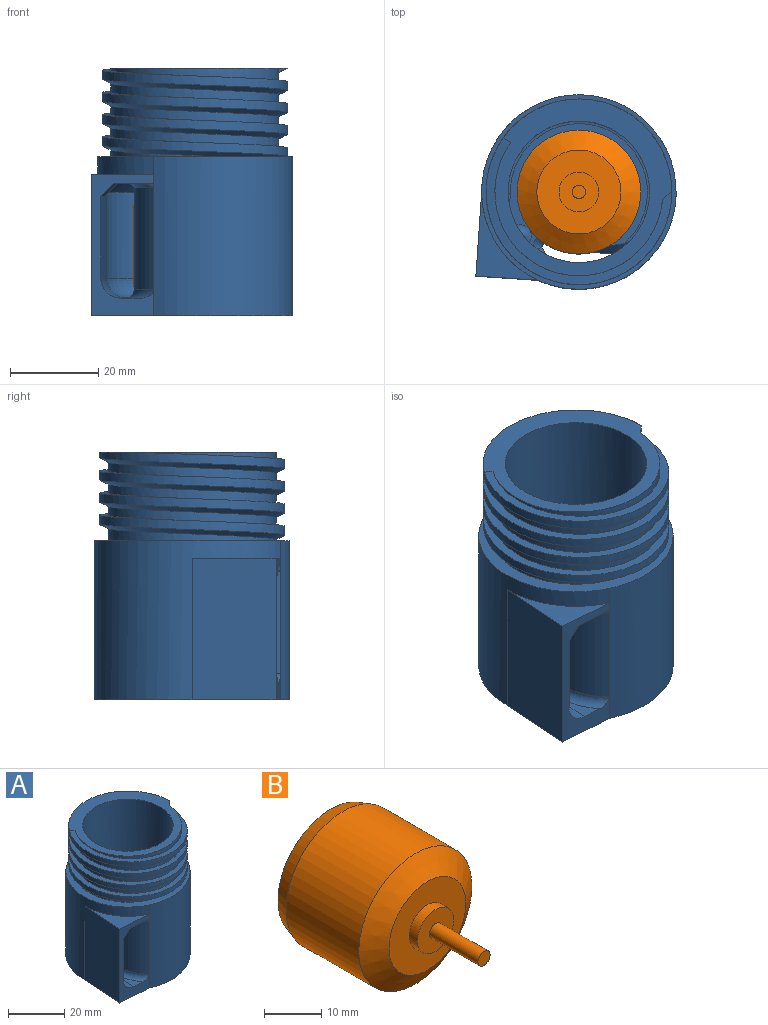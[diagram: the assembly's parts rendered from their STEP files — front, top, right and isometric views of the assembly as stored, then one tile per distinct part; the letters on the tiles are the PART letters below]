
ASSEMBLY  parts=2 mates=1
PART A: 61 faces, bbox 45.4x48.6x56.4 mm
  f0: cylinder r=22mm len=2.45mm, axis (0,0,-1), area 1.4mm2, adj f3,f28,f59
  f1: cylinder r=22mm len=44mm, axis (0,0,-1), area 4176.6mm2, adj f8,f12,f14,f19,f20,f28,f47
  f2: plane 8.06x4.55mm, normal (0.71,-0.05,-0.71), area 44.5mm2, adj f9,f21,f50,f58
  f3: cone r=18mm half-angle=45deg, axis (0,0,1), area 14.6mm2, adj f0,f4,f27,f59
  f4: cone r=3.5mm half-angle=45deg, axis (0,0,1), area 5.8mm2, adj f3,f9,f30,f49,f57,f58,f59
  f5: plane 0.1x0.05mm, normal (0,-1,0), area 0mm2, adj f52,f53,f54
  f6: bspline ~48.5x42mm, area 903.6mm2, adj f7,f51,f52,f55
  f7: cylinder r=21mm len=42mm, axis (0,0,-1), area 1025.8mm2, adj f6,f8,f52,f53,f55
  f8: plane 44x44mm, normal (0,0,1), area 357.7mm2, adj f1,f7,f12,f28,f51,f53,f55
  f9: plane 7.94x1.97mm, normal (0,0,-1), area 5.8mm2, adj f2,f4,f49,f58
  f10: plane 0.48x0.36mm, normal (0,0,1), area 0mm2, adj f26,f30,f49
  f11: plane 0.02x0mm, normal (0,0,1), area 0mm2, adj f12,f20,f28
  f12: plane 32x0mm, normal (-1,0,0), area 0mm2, adj f1,f8,f11,f28
  f13: plane 35.26x32.31mm, normal (0,0,1), area 647.2mm2, adj f15,f16,f17,f18,f20,f29,f35,f36
  f14: plane 45.3x44mm, normal (0,0,-1), area 1423.8mm2, adj f1,f15,f16,f17,f18,f19,f20,f22
  f15: cylinder r=2.12mm len=4.25mm, axis (0,0,1), area 53.4mm2, adj f13,f14
  f16: cylinder r=2.12mm len=4.25mm, axis (0,0,1), area 53.4mm2, adj f13,f14
  f17: cylinder r=2.12mm len=4.25mm, axis (0,0,1), area 53.4mm2, adj f13,f14
  f18: cylinder r=2.12mm len=4.25mm, axis (0,0,1), area 53.4mm2, adj f13,f14
  f19: plane 32x19mm, normal (-1,0.07,0), area 609.3mm2, adj f1,f14,f20,f47
  f20: plane 32x14.03mm, normal (-0.07,-1,0), area 146.6mm2, adj f1,f11,f13,f14,f19,f21,f28,f36
  f21: plane 19.5x19mm, normal (1,-0.07,0), area 360mm2, adj f2,f20,f22,f36,f58,f60
  f22: cylinder r=20mm len=40mm, axis (0,0,-1), area 1992.3mm2, adj f14,f21,f29,f33,f34,f35,f44,f50
  f23: cylinder r=15mm len=11.2mm, axis (0,0,1), area 24.3mm2, adj f14,f31,f34,f38,f39
  f24: cylinder r=14mm len=11.1mm, axis (0,0,1), area 23.7mm2, adj f14,f31,f32,f41
  f25: cylinder r=15mm len=8.24mm, axis (0,0,1), area 23.4mm2, adj f14,f32,f33,f43
  f26: plane 26.84x0.4mm, normal (0.82,0.57,0), area 11.6mm2, adj f10,f29,f30,f46
  f27: cylinder r=15mm len=23mm, axis (0,0,-1), area 259.8mm2, adj f3,f28,f30,f45
  f28: plane 32x0.02mm, normal (-0.01,-1,0), area 0.1mm2, adj f0,f1,f8,f11,f12,f20,f27,f45
  f29: cylinder r=15mm len=29.95mm, axis (0,0,-1), area 443.9mm2, adj f13,f22,f26,f43,f44,f46,f50
  f30: cylinder r=0.5mm len=26mm, axis (0,0,-1), area 30.1mm2, adj f4,f10,f26,f27,f46,f49
  f31: cylinder r=0.5mm len=2.04mm, axis (0,0,-1), area 0.5mm2, adj f14,f23,f24,f40
  f32: cylinder r=0.5mm len=2.04mm, axis (0,0,1), area 2.6mm2, adj f14,f24,f25,f42
  f33: cylinder r=0.5mm len=2.04mm, axis (0,0,-1), area 0.4mm2, adj f14,f22,f25,f44
  f34: cylinder r=0.5mm len=8.5mm, axis (0,0,1), area 6.2mm2, adj f14,f22,f23,f37
  f35: torus R=15.5mm, axis (0,0,1), area 489mm2, adj f13,f22,f36,f37,f38
  f36: cylinder r=4.5mm len=19.48mm, axis (0.07,1,0), area 135.2mm2, adj f13,f20,f21,f35
  f37: bspline ~6.22x3.3mm, area 7.5mm2, adj f34,f35,f38
  f38: bspline ~4.7x3.72mm, area 12.2mm2, adj f23,f35,f37,f39
  f39: cone r=13.04mm half-angle=45deg, axis (0,0,-1), area 18.2mm2, adj f13,f23,f38,f40
  f40: cone r=2.46mm half-angle=45deg, axis (0,0,1), area 2mm2, adj f13,f31,f39,f41
  f41: cone r=12.04mm half-angle=45deg, axis (0,0,-1), area 29.8mm2, adj f13,f24,f40,f42
  f42: cone r=2.46mm half-angle=45deg, axis (0,0,1), area 10.6mm2, adj f13,f32,f41,f43
  f43: cone r=15mm half-angle=45deg, axis (0,0,1), area 22.2mm2, adj f13,f25,f29,f42,f44
  f44: cone r=2.46mm half-angle=45deg, axis (0,0,1), area 0mm2, adj f22,f29,f33,f43
  f45: torus R=17mm, axis (0,0,1), area 34.7mm2, adj f13,f20,f27,f28,f46
  f46: torus R=2.5mm, axis (0,0,1), area 14.2mm2, adj f13,f26,f29,f30,f45
  f47: plane 19.95x14.03mm, normal (0,0,1), area 78.4mm2, adj f1,f19,f20,f56
  f48: extruded ~5.2x5.2mm, area 64.3mm2, adj f13,f14
  f49: cylinder r=16mm len=32mm, axis (0,0,-1), area 2417.7mm2, adj f4,f9,f10,f30,f50,f52
  f50: cone r=20mm half-angle=45deg, axis (0,0,-1), area 525.2mm2, adj f2,f22,f29,f49
  f51: cylinder r=19mm len=38mm, axis (0,0,-1), area 1010.4mm2, adj f6,f8,f52,f53,f54,f55
  f52: plane 40x40mm, normal (0,0,1), area 432.3mm2, adj f5,f6,f7,f49,f51,f54
  f53: bspline ~48.5x42mm, area 1098.8mm2, adj f5,f7,f8,f51,f54
  f54: plane 2.09x1.91mm, normal (0.67,-0.74,0), area 1.4mm2, adj f5,f51,f52,f53
  f55: plane 2.11x2mm, normal (0,0.71,0.71), area 5.7mm2, adj f6,f7,f8,f51
  f56: cylinder r=15mm len=2mm, axis (0,0,-1), area 0mm2, adj f20,f28,f47,f59
  f57: cylinder r=15mm len=0.05mm, axis (0,0,-1), area 0mm2, adj f4,f58,f59
  f58: plane 6.83x5mm, normal (0.07,1,0), area 7.4mm2, adj f2,f4,f9,f21,f57,f59,f60
  f59: plane 11.84x9.03mm, normal (0,0,-1), area 50mm2, adj f0,f3,f4,f20,f56,f57,f58,f60
  f60: plane 11.43x3.76mm, normal (0.71,-0.05,-0.71), area 47.7mm2, adj f20,f21,f58,f59
PART B: 17 faces, bbox 28x38x28 mm
  f0: plane 3x3mm, normal (0,-1,0), area 7.1mm2, adj f1
  f1: cylinder r=1.5mm len=12mm, axis (0,1,0), area 113.1mm2, adj f0,f2
  f2: plane 9x9mm, normal (0,-1,0), area 56.5mm2, adj f1,f3
  f3: cylinder r=4.5mm len=9mm, axis (0,1,0), area 56.5mm2, adj f2,f4
  f4: plane 19x19mm, normal (0,-1,0), area 219.9mm2, adj f3,f5
  f5: cone r=9.5mm half-angle=56.3deg, axis (0,1,0), area 399.3mm2, adj f4,f6
  f6: cylinder r=14mm len=28mm, axis (0,1,0), area 1583.4mm2, adj f5,f7
  f7: cone r=14mm half-angle=18.4deg, axis (0,-1,0), area 268.2mm2, adj f6,f8
  f8: plane 26x26mm, normal (0,1,0), area 502.7mm2, adj f7,f9,f11,f13,f15
  f9: cylinder r=1.5mm len=3mm, axis (0,1,0), area 18.8mm2, adj f8,f10
  f10: plane 3x3mm, normal (0,1,0), area 7.1mm2, adj f9
  f11: cylinder r=1.5mm len=3mm, axis (0,1,0), area 18.8mm2, adj f8,f12
  f12: plane 3x3mm, normal (0,1,0), area 7.1mm2, adj f11
  f13: cylinder r=1.5mm len=3mm, axis (0,1,0), area 18.8mm2, adj f8,f14
  f14: plane 3x3mm, normal (0,1,0), area 7.1mm2, adj f13
  f15: cylinder r=1.5mm len=3mm, axis (0,1,0), area 18.8mm2, adj f8,f16
  f16: plane 3x3mm, normal (0,1,0), area 7.1mm2, adj f15
PLACE A at identity fixed
PLACE B rot(axis=(0,-0.71,0.71),180deg) t=(0,0,2)mm
MATE fastened B.f11 <-> A.f15  axis (0,0,-1) through (0,9.5,4)mm
